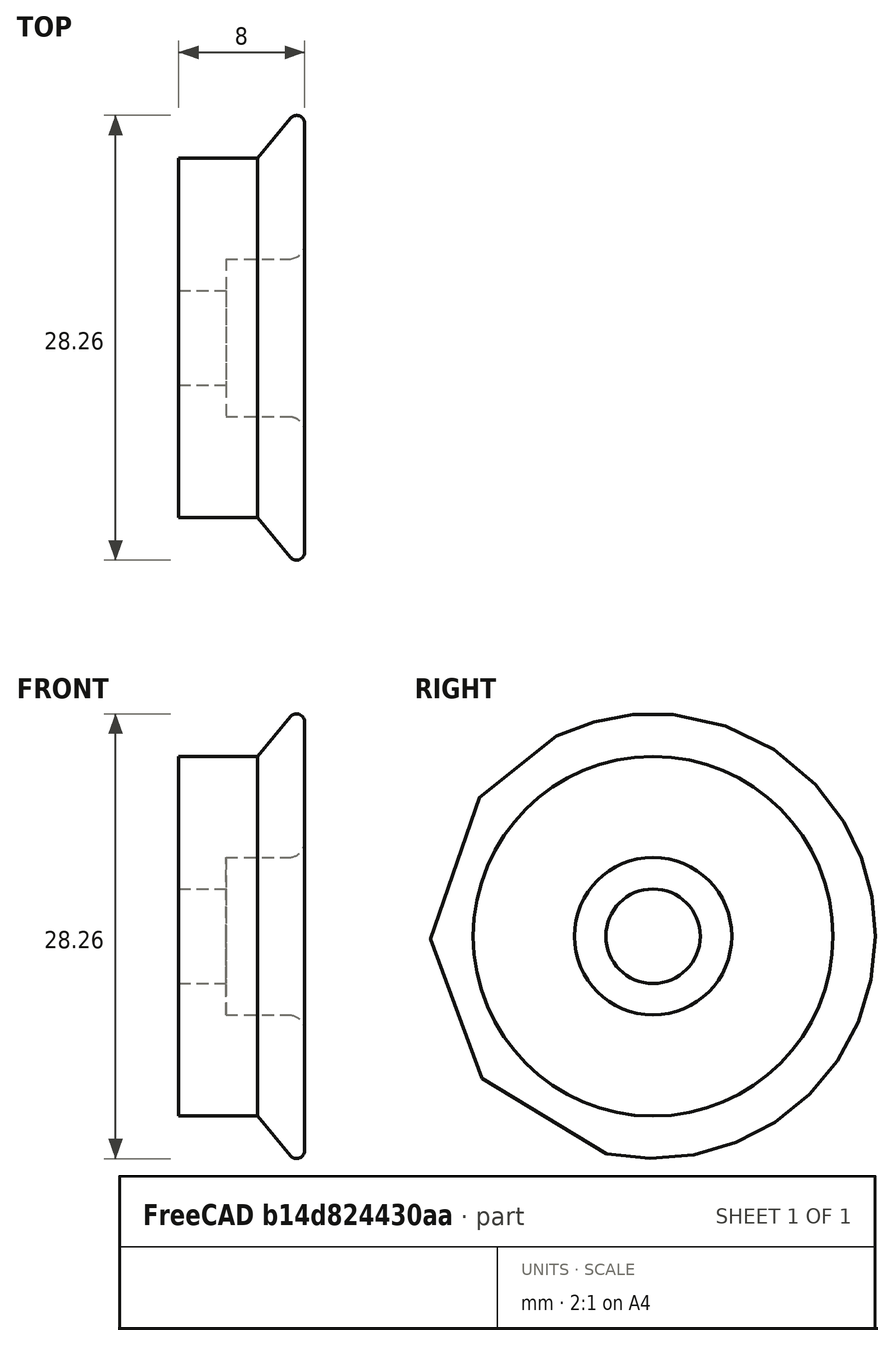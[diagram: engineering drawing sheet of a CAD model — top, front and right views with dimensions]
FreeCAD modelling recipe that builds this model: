
FCSTD DOCUMENT
Label: SpoolCoasterWheel
objects: Sketcher::SketchObject×2, Part::Fillet×2, Part::Revolution×1
note: 5 computed .brp shape members not serialized (recipe doc carries the construction recipe); baked Part::Feature solids carry a one-line shape summary decoded from their .brp

FEATURE [Sketcher::SketchObject] Sketch
  sketch-geometry (7):
    g0: LineSegment StartX=-4.96478 StartY=3 StartZ=0 EndX=-4.96478 EndY=5 EndZ=0
    g1: LineSegment StartX=-4.96478 StartY=5 StartZ=0 EndX=0.035217 EndY=5 EndZ=0
    g2: LineSegment StartX=0.035217 StartY=5 StartZ=0 EndX=0.035217 EndY=15 EndZ=0
    g3: LineSegment StartX=0.035217 StartY=15 StartZ=0 EndX=-2.96478 EndY=11.4247 EndZ=0
    g4: LineSegment StartX=-2.96478 StartY=11.4247 StartZ=0 EndX=-7.96478 EndY=11.4247 EndZ=0
    g5: LineSegment StartX=-7.96478 StartY=11.4247 StartZ=0 EndX=-7.96478 EndY=3 EndZ=0
    g6: LineSegment StartX=-7.96478 StartY=3 StartZ=0 EndX=-4.96478 EndY=3 EndZ=0
  constraints (21):
    c: Vertical(g0)
    c: Coincident(g0,g1)
    c: Horizontal(g1)
    c: Coincident(g1,g2)
    c: Vertical(g2)
    c: Coincident(g2,g3)
    c: Coincident(g3,g4)
    c: Coincident(g4,g5)
    c: Vertical(g5)
    c: Coincident(g5,g6)
    c: Coincident(g6,g0)
    c: Horizontal(g6)
    c: Distance(g1) = 5
    c: Distance(g6) = 3
    c: Distance(g0) = 2
    c: Distance(g2) = 10
    c: Horizontal(g4)
    c: Angle(g3) = -2.26893
    c: Distance(g4) = 5
    c: DistanceX(g1) = 0.035217
    c: DistanceY(g1) = 5
FEATURE [Part::Revolution] Revolve
  Angle = 360
  Axis = (1,0,0)
  Base = (0,0,0)
  Source = -> Sketch
FEATURE [Part::Fillet] Fillet
  Base = -> Revolve
  Edges = 1 edges r=1: [Edge3]
FEATURE [Part::Fillet] Fillet001
  Base = -> Fillet
  Edges = 1 edges r=0.5: [Edge7]
FEATURE [Sketcher::SketchObject] Sketch001
  Placement = pos=(0.035217,0,0) rot=(0.57735,-0.57735,-0.57735;2.0944rad)
  Support = -> Fillet001 [Face1]
  sketch-geometry (1):
    g0: Circle CenterX=0 CenterY=9 CenterZ=0 NormalX=0 NormalY=0 NormalZ=1 Radius=1.5
  constraints (3):
    c: DistanceX(g0) = 0
    c: DistanceY(g0) = 9
    c: Radius(g0) = 1.5
